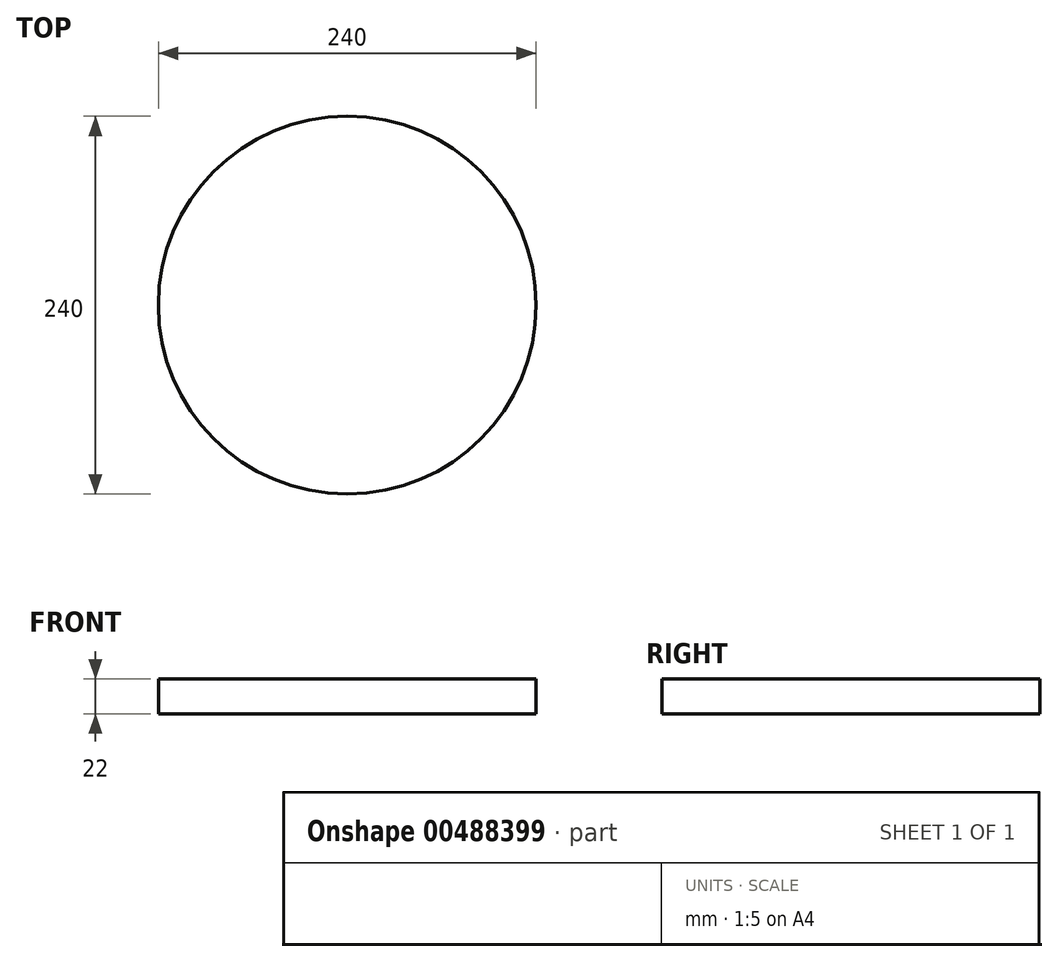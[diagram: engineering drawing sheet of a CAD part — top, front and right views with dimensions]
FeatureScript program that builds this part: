
annotation { "Feature Type Name" : "Feature", "Feature Type Description" : "" }
export const myFeature = defineFeature(function(context is Context, id is Id, definition is map)
    precondition{}
    {
        {
            var Q0;
            Q0=qCreatedBy(makeId("Top.planeOp"),FACE);
            var sketch = newSketch(context, id + "F0", { "sketchPlane" : qUnion([Q0])});
            skCircle(sketch, "E0", {"center": v(0, 0) * mm, "radius": 120 * mm});
            skCircle(sketch, "E1", {"center": v(0, 0) * mm, "radius": 100 * mm});
            skSolve(sketch);
        }
        {
            var Q0;
            Q0=makeQuery(id+"F0.imprint","IMPRINT",FACE,{"disambiguationData":[TD([[makeQuery(id+"F0.imprint","IMPRINT",EDGE,{"derivedFrom":sQuery(id+"F0.wireOp",EDGE,"E0")}),1.0]])]});
            var Q1;
            Q1=makeQuery(id+"F0.imprint","IMPRINT",FACE,{"disambiguationData":[TD([[makeQuery(id+"F0.imprint","IMPRINT",EDGE,{"derivedFrom":sQuery(id+"F0.wireOp",EDGE,"E1")}),1.0]])]});
            extrude(context, id + "F1", {"entities" : qUnion([Q0, Q1]), "oppositeDirection" : true, "depth" : 9 * mm});
        }
        {
            var Q0;
            Q0=makeQuery(id+"F0.imprint","IMPRINT",FACE,{"disambiguationData":[TD([[makeQuery(id+"F0.imprint","IMPRINT",EDGE,{"derivedFrom":sQuery(id+"F0.wireOp",EDGE,"E1")}),1.0]])]});
            extrude(context, id + "F2", {"entities" : qUnion([Q0]), "depth" : 4 * mm});
        }
        {
            var Q0;
            Q0=makeQuery(id+"F0.imprint","IMPRINT",FACE,{"disambiguationData":[TD([[makeQuery(id+"F0.imprint","IMPRINT",EDGE,{"derivedFrom":sQuery(id+"F0.wireOp",EDGE,"E0")}),1.0]])]});
            extrude(context, id + "F3", {"entities" : qUnion([Q0]), "operationType" : NewBodyOperationType.ADD, "depth" : 13 * mm});
        }
        {
            var Q0;
            Q0=makeQuery(id+"F2.opExtrude","CAP_FACE",FACE,{"disambiguationData":[OSD([sQuery(id+"F0.wireOp",EDGE,"E1")])],"isStart":false});
            extrude(context, id + "F4", {"entities" : qUnion([Q0]), "operationType" : NewBodyOperationType.ADD, "depth" : 9 * mm});
        }
    });
